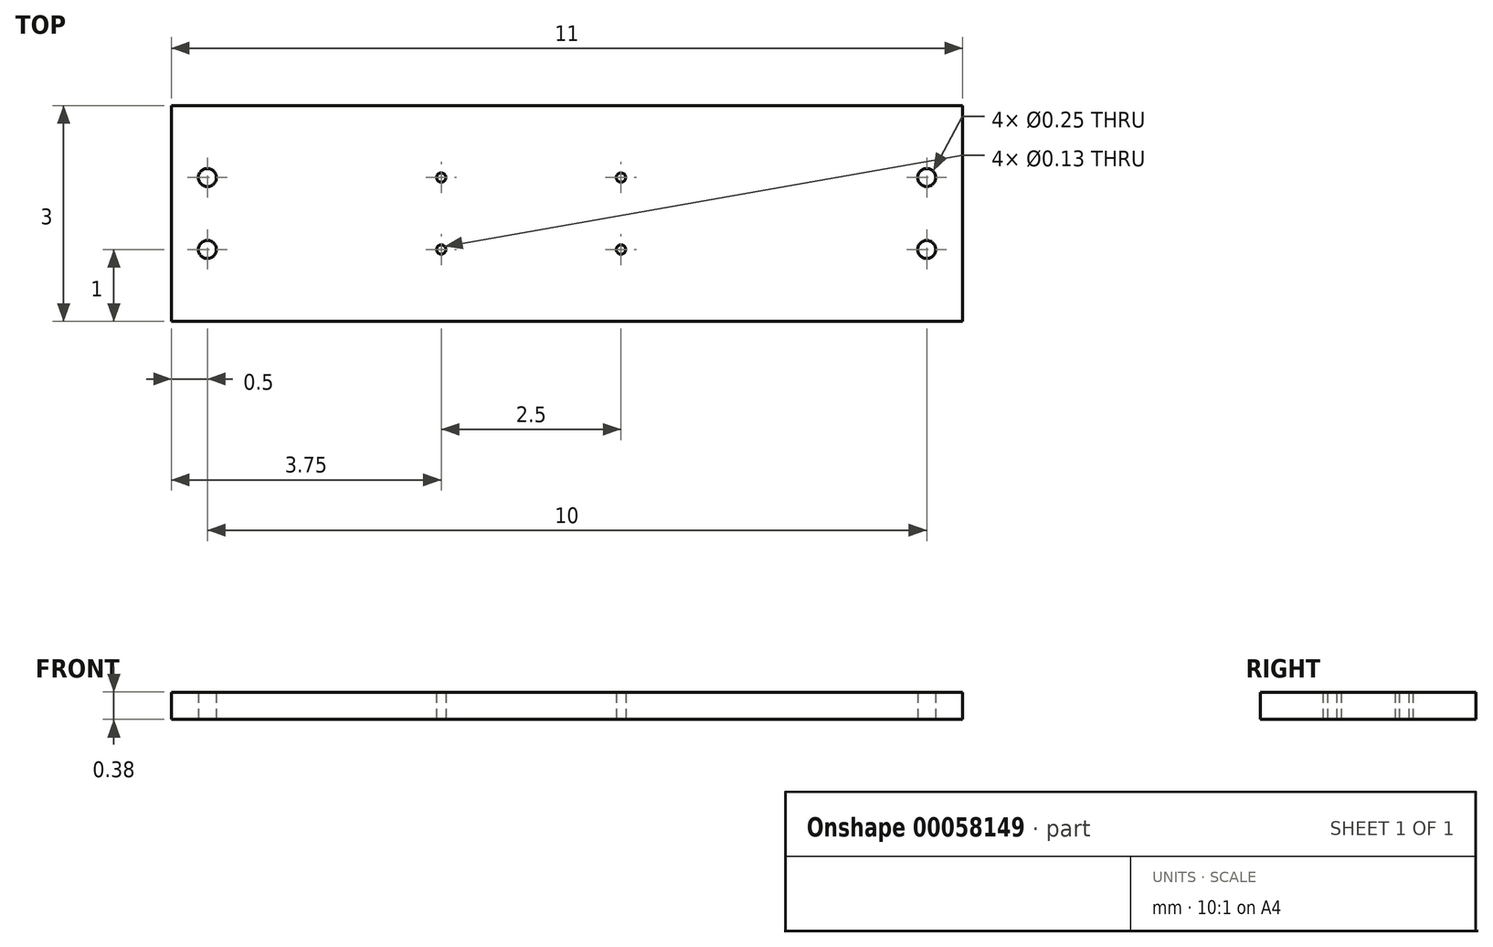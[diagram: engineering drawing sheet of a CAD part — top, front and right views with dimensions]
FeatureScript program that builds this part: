
annotation { "Feature Type Name" : "Feature", "Feature Type Description" : "" }
export const myFeature = defineFeature(function(context is Context, id is Id, definition is map)
    precondition{}
    {
        {
            var Q0;
            Q0=qCreatedBy(makeId("Top.planeOp"),FACE);
            var sketch = newSketch(context, id + "F0", { "sketchPlane" : qUnion([Q0])});
            skLineSegment(sketch, "E0.bottom", {"start": v(-5.5, 1.5) * mm, "end": v(5.5, 1.5) * mm});
            skLineSegment(sketch, "E0.top", {"start": v(-5.5, -1.5) * mm, "end": v(5.5, -1.5) * mm});
            skLineSegment(sketch, "E0.left", {"start": v(-5.5, 1.5) * mm, "end": v(-5.5, -1.5) * mm});
            skLineSegment(sketch, "E0.right", {"start": v(5.5, 1.5) * mm, "end": v(5.5, -1.5) * mm});
            skCircle(sketch, "E1", {"center": v(-5, 0.5) * mm, "radius": 0.12 * mm});
            skCircle(sketch, "E2", {"center": v(-5, -0.5) * mm, "radius": 0.12 * mm});
            skCircle(sketch, "E3", {"center": v(-1.75, 0.5) * mm, "radius": 0.07 * mm});
            skCircle(sketch, "E4", {"center": v(-1.75, -0.5) * mm, "radius": 0.07 * mm});
            skCircle(sketch, "E5", {"center": v(0.75, 0.5) * mm, "radius": 0.07 * mm});
            skCircle(sketch, "E6", {"center": v(0.75, -0.5) * mm, "radius": 0.07 * mm});
            skCircle(sketch, "E7", {"center": v(5, 0.5) * mm, "radius": 0.12 * mm});
            skCircle(sketch, "E8", {"center": v(5, -0.5) * mm, "radius": 0.12 * mm});
            skSolve(sketch);
        }
        {
            var Q0;
            Q0=makeQuery(id+"F0.imprint","IMPRINT",FACE,{"disambiguationData":[TD([[makeQuery(id+"F0.imprint","IMPRINT",EDGE,{"derivedFrom":sQuery(id+"F0.wireOp",EDGE,"E0.bottom")}),-1.0]])]});
            extrude(context, id + "F1", {"entities" : qUnion([Q0]), "endBound" : BoundingType.SYMMETRIC, "depth" : 0.38 * mm});
        }
    });
